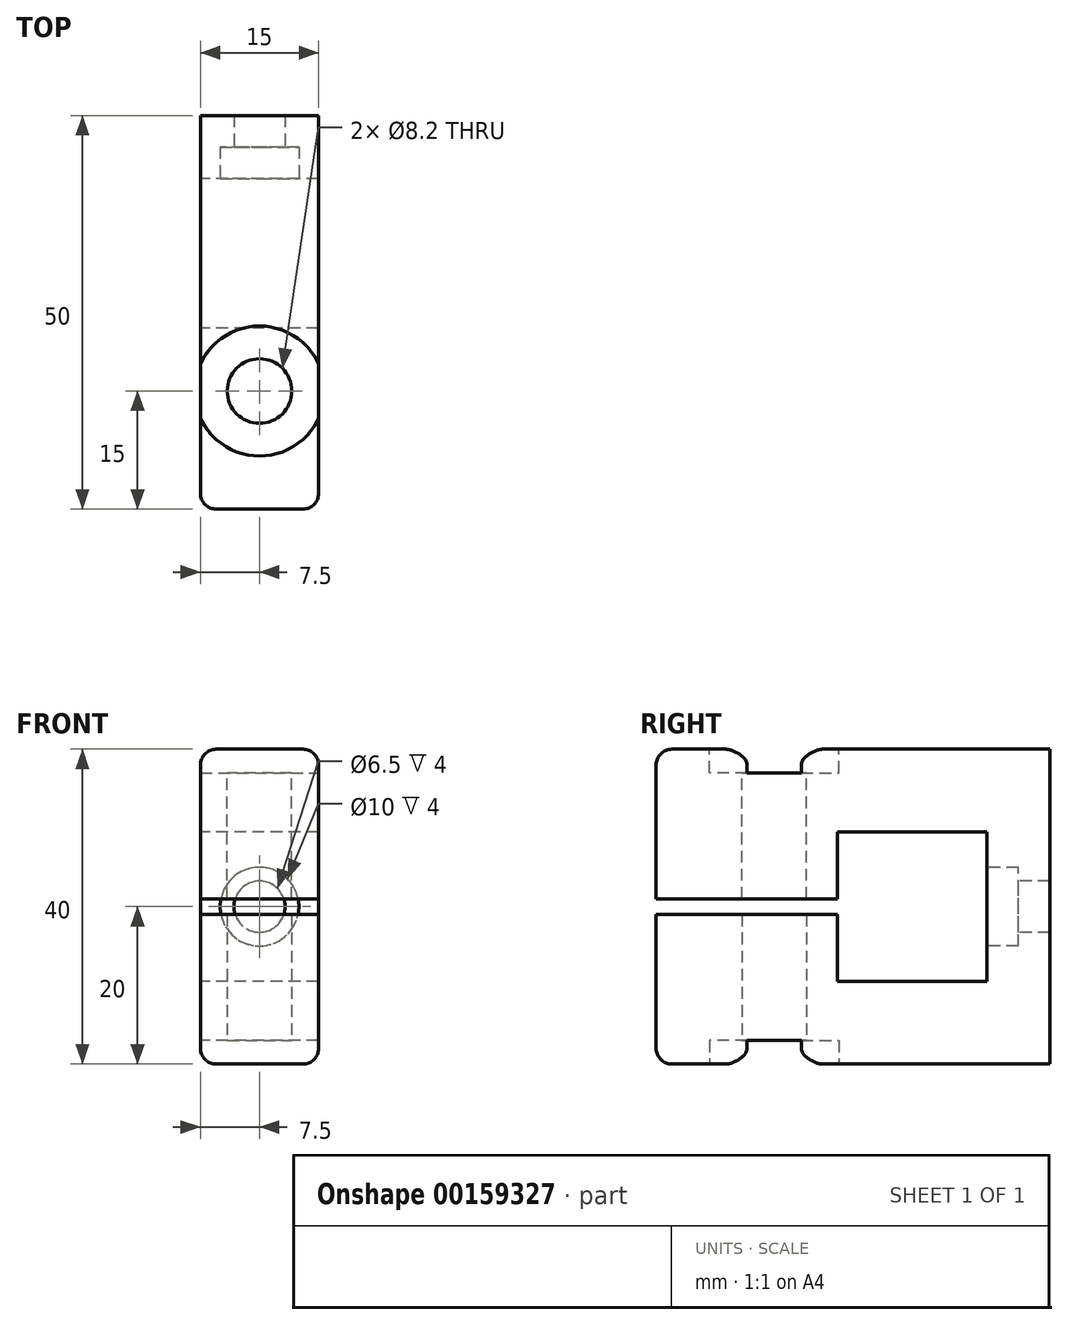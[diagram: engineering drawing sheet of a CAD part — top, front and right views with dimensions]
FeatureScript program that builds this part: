
annotation { "Feature Type Name" : "Feature", "Feature Type Description" : "" }
export const myFeature = defineFeature(function(context is Context, id is Id, definition is map)
    precondition{}
    {
        {
            var Q0;
            Q0=qCreatedBy(makeId("Right.planeOp"),FACE);
            var sketch = newSketch(context, id + "F0", { "sketchPlane" : qUnion([Q0])});
            skLineSegment(sketch, "E0.bottom", {"start": v(9.5, -9.5) * mm, "end": v(-9.5, -9.5) * mm});
            skLineSegment(sketch, "E0.top", {"start": v(9.5, 9.5) * mm, "end": v(-9.5, 9.5) * mm});
            skLineSegment(sketch, "E0.left", {"start": v(9.5, -9.5) * mm, "end": v(9.5, 9.5) * mm});
            skLineSegment(sketch, "E0.right", {"start": v(-9.5, -9.5) * mm, "end": v(-9.5, -1) * mm});
            skPoint(sketch, "E0.middle", {"position": v(0, 0) * mm});
            skLineSegment(sketch, "E1.left", {"start": v(17.5, -20) * mm, "end": v(17.5, 20) * mm});
            skLineSegment(sketch, "E2", {"start": v(17.5, 20) * mm, "end": v(-32.5, 20) * mm});
            skLineSegment(sketch, "E3", {"start": v(-32.5, 20) * mm, "end": v(-32.5, 1) * mm});
            skLineSegment(sketch, "E4", {"start": v(-32.5, -20) * mm, "end": v(17.5, -20) * mm});
            skLineSegment(sketch, "E5", {"start": v(0, 0) * mm, "end": v(0, 29.36) * mm, "construction": true});
            skLineSegment(sketch, "E6", {"start": v(0, 0) * mm, "end": v(0, -29.79) * mm, "construction": true});
            skLineSegment(sketch, "E7", {"start": v(-9.5, -1) * mm, "end": v(-32.5, -1) * mm});
            skLineSegment(sketch, "E8", {"start": v(-32.5, 1) * mm, "end": v(-9.5, 1) * mm});
            skLineSegment(sketch, "E9.trimOffspring", {"start": v(-9.5, 1) * mm, "end": v(-9.5, 9.5) * mm});
            skLineSegment(sketch, "E10.trimOffspring", {"start": v(-32.5, -1) * mm, "end": v(-32.5, -20) * mm});
            skSolve(sketch);
        }
        {
            var Q0;
            Q0=qSketchRegion(id+"F0",true);
            extrude(context, id + "F1", {"entities" : qUnion([Q0]), "depth" : 15 * mm});
        }
        {
            var Q0;
            Q0=makeQuery(id+"F1.opExtrude","SWEPT_FACE",FACE,{"disambiguationData":[OSD([sQuery(id+"F0.wireOp",EDGE,"E0.left")])]});
            var sketch = newSketch(context, id + "F2", { "sketchPlane" : qUnion([Q0])});
            skPoint(sketch, "E11", {"position": v(7.5, 0) * mm});
            skPoint(sketch, "E11.positionSnap0", {"position": v(7.5, 9.5) * mm});
            skSolve(sketch);
        }
        {
            var Q0;
            Q0=sQuery(id+"F2.wireOp",VERTEX,"E11");
            var Q1;
            Q1=makeQuery(id+"F1.opExtrude","SWEPT_BODY",BODY,{"disambiguationData":[OSD([sQuery(id+"F0.wireOp",EDGE,"E0.bottom"),sQuery(id+"F0.wireOp",EDGE,"E0.top"),sQuery(id+"F0.wireOp",EDGE,"E0.left"),sQuery(id+"F0.wireOp",EDGE,"E0.right"),sQuery(id+"F0.wireOp",EDGE,"E1.bottom"),sQuery(id+"F0.wireOp",EDGE,"E1.top"),sQuery(id+"F0.wireOp",EDGE,"E1.left"),sQuery(id+"F0.wireOp",EDGE,"E1.right")])]});
            hole(context, id + "F3", {"style" : HoleStyle.C_BORE, "endStyle" : HoleEndStyle.THROUGH, "holeDiameter" : 6.5 * mm, "cBoreDiameter" : 10 * mm, "cBoreDepth" : 4 * mm, "locations" : qUnion([Q0]), "scope" : qUnion([Q1]), "isTappedThrough" : true});
        }
        {
            var Q0;
            Q0=makeQuery(id+"F1.opExtrude","SWEPT_FACE",FACE,{"disambiguationData":[OSD([sQuery(id+"F0.wireOp",EDGE,"E2")])]});
            var sketch = newSketch(context, id + "F4", { "sketchPlane" : qUnion([Q0])});
            skPoint(sketch, "E12", {"position": v(7.5, -17.5) * mm});
            skPoint(sketch, "E12.positionSnap1", {"position": v(7.5, -32.5) * mm});
            skSolve(sketch);
        }
        {
            var Q0;
            Q0=sQuery(id+"F4.wireOp",VERTEX,"E12");
            var Q1;
            Q1=makeQuery(id+"F1.opExtrude","SWEPT_BODY",BODY,{"disambiguationData":[OSD([sQuery(id+"F0.wireOp",EDGE,"E0.bottom"),sQuery(id+"F0.wireOp",EDGE,"E0.top"),sQuery(id+"F0.wireOp",EDGE,"E0.left"),sQuery(id+"F0.wireOp",EDGE,"E0.right"),sQuery(id+"F0.wireOp",EDGE,"E1.bottom"),sQuery(id+"F0.wireOp",EDGE,"E1.top"),sQuery(id+"F0.wireOp",EDGE,"E1.left"),sQuery(id+"F0.wireOp",EDGE,"E1.right")])]});
            hole(context, id + "F5", {"style" : HoleStyle.C_BORE, "endStyle" : HoleEndStyle.BLIND, "holeDiameter" : 8.2 * mm, "cBoreDiameter" : 16.5 * mm, "cBoreDepth" : 3 * mm, "holeDepth" : 20 * mm, "locations" : qUnion([Q0]), "scope" : qUnion([Q1])});
        }
        {
            var Q0;
            Q0=makeQuery(id+"F1.opExtrude","SWEPT_FACE",FACE,{"disambiguationData":[OSD([sQuery(id+"F0.wireOp",EDGE,"E4")])]});
            var sketch = newSketch(context, id + "F6", { "sketchPlane" : qUnion([Q0])});
            skPoint(sketch, "E13", {"position": v(7.5, 17.5) * mm});
            skPoint(sketch, "E13.positionSnap1", {"position": v(7.5, 32.5) * mm});
            skSolve(sketch);
        }
        {
            var Q0;
            Q0=sQuery(id+"F6.wireOp",VERTEX,"E13");
            var Q1;
            Q1=makeQuery(id+"F1.opExtrude","SWEPT_BODY",BODY,{"disambiguationData":[OSD([sQuery(id+"F0.wireOp",EDGE,"E0.bottom"),sQuery(id+"F0.wireOp",EDGE,"E0.top"),sQuery(id+"F0.wireOp",EDGE,"E0.left"),sQuery(id+"F0.wireOp",EDGE,"E0.right"),sQuery(id+"F0.wireOp",EDGE,"E1.bottom"),sQuery(id+"F0.wireOp",EDGE,"E1.top"),sQuery(id+"F0.wireOp",EDGE,"E1.left"),sQuery(id+"F0.wireOp",EDGE,"E1.right")])]});
            hole(context, id + "F7", {"style" : HoleStyle.C_BORE, "endStyle" : HoleEndStyle.BLIND, "holeDiameter" : 8.2 * mm, "cBoreDiameter" : 16.5 * mm, "cBoreDepth" : 3 * mm, "holeDepth" : 20 * mm, "locations" : qUnion([Q0]), "scope" : qUnion([Q1])});
        }
        {
            var Q0;
            Q0=makeQuery(id+"F1.opExtrude","SWEPT_EDGE",EDGE,{"disambiguationData":[OSD([sQuery(id+"F0.wireOp",EDGE,"E2"),sQuery(id+"F0.wireOp",EDGE,"E3")])]});
            var Q1;
            Q1=makeQuery(id+"F1.opExtrude","CAP_EDGE",EDGE,{"disambiguationData":[OSD([sQuery(id+"F0.wireOp",EDGE,"E2")])],"isStart":true});
            var Q2;
            Q2=makeQuery(id+"F1.opExtrude","CAP_EDGE",EDGE,{"disambiguationData":[OSD([sQuery(id+"F0.wireOp",EDGE,"E2")])],"isStart":false});
            var Q3;
            Q3=makeQuery(id+"F1.opExtrude","CAP_EDGE",EDGE,{"disambiguationData":[OSD([sQuery(id+"F0.wireOp",EDGE,"E4")])],"isStart":true});
            var Q4;
            Q4=makeQuery(id+"F1.opExtrude","SWEPT_EDGE",EDGE,{"disambiguationData":[OSD([sQuery(id+"F0.wireOp",EDGE,"E4"),sQuery(id+"F0.wireOp",EDGE,"E10.trimOffspring")])]});
            var Q5;
            Q5=makeQuery(id+"F1.opExtrude","CAP_EDGE",EDGE,{"disambiguationData":[OSD([sQuery(id+"F0.wireOp",EDGE,"E4")])],"isStart":false});
            var Q6;
            Q6=makeQuery(id+"F1.opExtrude","CAP_EDGE",EDGE,{"disambiguationData":[OSD([sQuery(id+"F0.wireOp",EDGE,"E3")])],"isStart":true});
            var Q7;
            Q7=makeQuery(id+"F1.opExtrude","CAP_EDGE",EDGE,{"disambiguationData":[OSD([sQuery(id+"F0.wireOp",EDGE,"E10.trimOffspring")])],"isStart":true});
            var Q8;
            Q8=makeQuery(id+"F1.opExtrude","CAP_EDGE",EDGE,{"disambiguationData":[OSD([sQuery(id+"F0.wireOp",EDGE,"E10.trimOffspring")])],"isStart":false});
            var Q9;
            Q9=makeQuery(id+"F1.opExtrude","CAP_EDGE",EDGE,{"disambiguationData":[OSD([sQuery(id+"F0.wireOp",EDGE,"E3")])],"isStart":false});
            fillet(context, id + "F8", {"entities" : qUnion([Q0, Q1, Q2, Q3, Q4, Q5, Q6, Q7, Q8, Q9]), "radius" : 2 * mm, "tangentPropagation" : true, "allowEdgeOverflow" : false});
        }
    });
